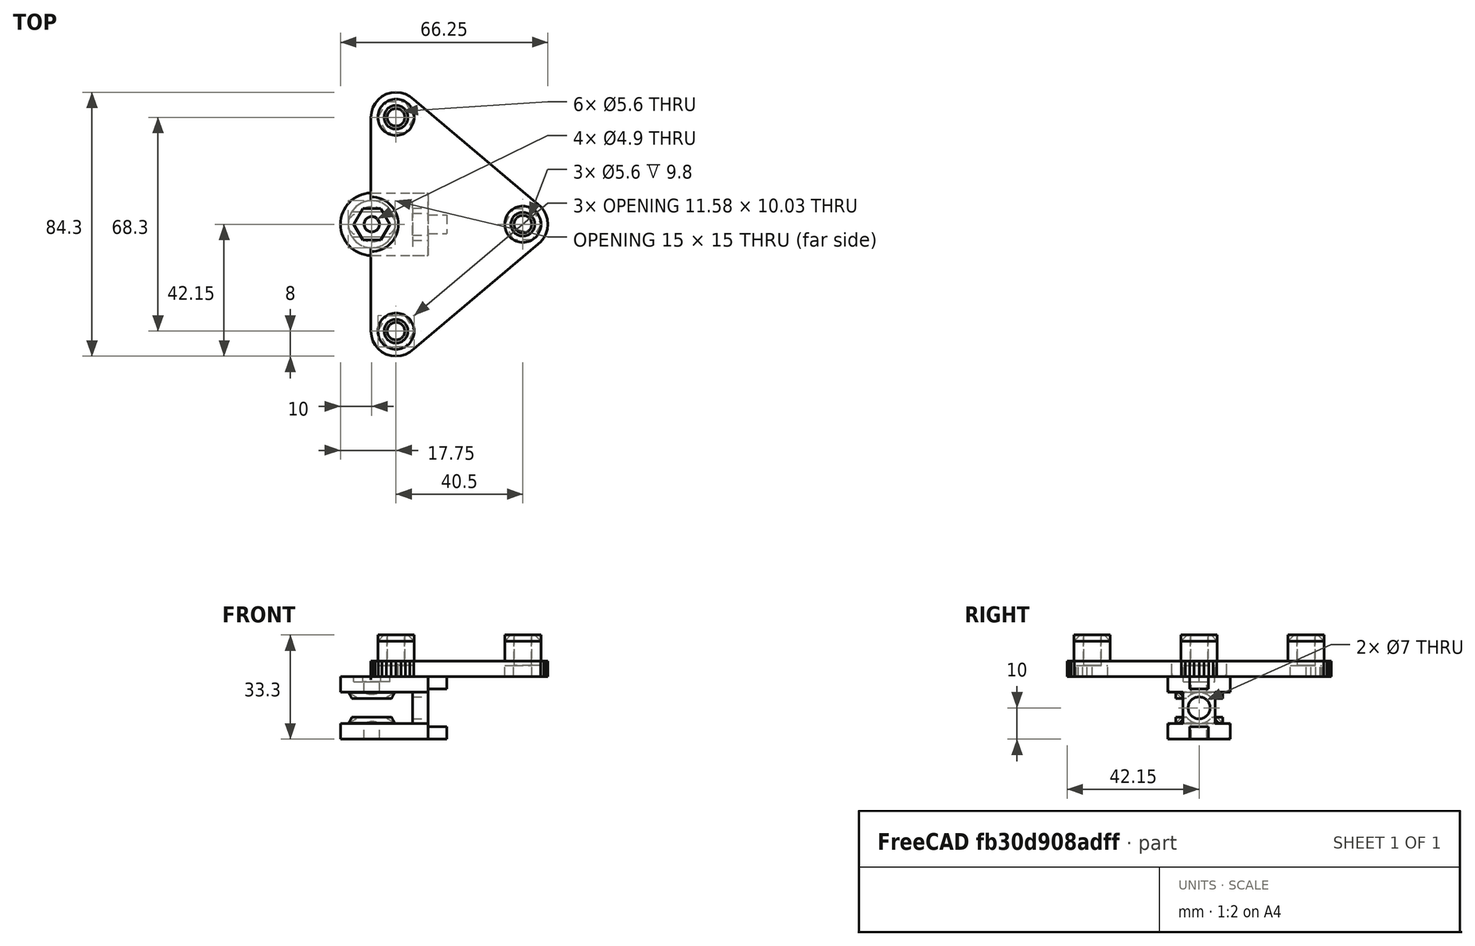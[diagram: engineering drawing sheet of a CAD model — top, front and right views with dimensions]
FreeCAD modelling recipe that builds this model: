
FCSTD DOCUMENT  (FreeCAD 0.19R24267 +99 (Git))
Label: carroZ_3
License: All rights reserved
LicenseURL: http://en.wikipedia.org/wiki/All_rights_reserved
objects: Part::Feature×36, Part::Cylinder×14, Part::Box×10, Part::Fillet×9, Part::Cut×8, Part::MultiFuse×8, Part::Chamfer×7, Part::Fuse×6, Part::Prism×4, Part::Part2DObjectPython×4, Part::FeaturePython×2, Part::Extrusion×1, Part::Common×1, App::DocumentObjectGroupPython×1, Part::Refine×1
note: 111 computed .brp shape members not serialized (recipe doc carries the construction recipe); baked Part::Feature solids carry a one-line shape summary decoded from their .brp

FEATURE [Part::Box] cube
  AttacherType = Attacher::AttachEngine3D
  Height = 5
  Length = 20
  Placement = pos=(-10,-10,0) rot=(0,0,1;0rad)
  Width = 20
FEATURE [Part::Cylinder] cylinder
  Angle = 360
  AttacherType = Attacher::AttachEngine3D
  Height = 100
  Placement = pos=(0,0,-50) rot=(0,0,1;0rad)
  Radius = 3.5
FEATURE [Part::Cut] difference
  Base = -> cube
  Tool = -> cylinder
FEATURE [Part::Box] cube001
  AttacherType = Attacher::AttachEngine3D
  Height = 11
  Length = 4
  Placement = pos=(6,-3,0) rot=(0,0,1;0rad)
  Width = 6
FEATURE [Part::Box] cube002
  AttacherType = Attacher::AttachEngine3D
  Height = 11
  Length = 4
  Placement = pos=(3,6,0) rot=(0,0,1;1.5708rad)
  Width = 6
FEATURE [Part::Box] cube003
  AttacherType = Attacher::AttachEngine3D
  Height = 11
  Length = 4
  Placement = pos=(-6,3,0) rot=(0,0,1;3.14159rad)
  Width = 6
FEATURE [Part::Box] cube004
  AttacherType = Attacher::AttachEngine3D
  Height = 11
  Length = 4
  Placement = pos=(-3,-6,0) rot=(0,0,-1;1.5708rad)
  Width = 6
FEATURE [Part::MultiFuse] Group
  Shapes = -> [cube001,cube002,cube003,cube004]
FEATURE [Part::Fuse] Group001
  Base = -> difference
  Tool = -> Group
FEATURE [Part::Box] cube005
  AttacherType = Attacher::AttachEngine3D
  Height = 100
  Length = 100
  Placement = pos=(5.15,-5,-50) rot=(0,0,1;0rad)
  Width = 10
FEATURE [Part::Box] cube006
  AttacherType = Attacher::AttachEngine3D
  Height = 100
  Length = 100
  Placement = pos=(-5.15,5,-50) rot=(0,0,1;3.14159rad)
  Width = 10
FEATURE [Part::Fuse] Group002
  Base = -> cube005
  Tool = -> cube006
FEATURE [Part::Cut] difference001
  Base = -> Group001
  Tool = -> Group002
FEATURE [Part::Box] cube007
  AttacherType = Attacher::AttachEngine3D
  Height = 13
  Length = 20
  Placement = pos=(-10,-10,-13) rot=(0,0,1;0rad)
  Width = 5
FEATURE [Part::Cylinder] cylinder001
  Angle = 360
  AttacherType = Attacher::AttachEngine3D
  Height = 5
  Placement = pos=(0,10,-13) rot=(1,0,0;1.5708rad)
  Radius = 10
FEATURE [Part::Cylinder] cylinder002
  Angle = 360
  AttacherType = Attacher::AttachEngine3D
  Height = 7
  Placement = pos=(0,10,-13) rot=(1,0,0;1.5708rad)
  Radius = 7.5
FEATURE [Part::MultiFuse] union
  Shapes = -> [cube007,cylinder001,cylinder002]
FEATURE [Part::Box] cube008
  AttacherType = Attacher::AttachEngine3D
  Height = 13
  Length = 20
  Placement = pos=(-10,-10,-13) rot=(0,0,1;0rad)
  Width = 5
FEATURE [Part::Cylinder] cylinder003
  Angle = 360
  AttacherType = Attacher::AttachEngine3D
  Height = 5
  Placement = pos=(0,10,-13) rot=(1,0,0;1.5708rad)
  Radius = 10
FEATURE [Part::Cylinder] cylinder004
  Angle = 360
  AttacherType = Attacher::AttachEngine3D
  Height = 7
  Placement = pos=(0,10,-13) rot=(1,0,0;1.5708rad)
  Radius = 7.5
FEATURE [Part::MultiFuse] union001
  Placement = pos=(0,0,0) rot=(0,0,1;3.14159rad)
  Shapes = -> [cube008,cylinder003,cylinder004]
FEATURE [Part::Fuse] Group003
  Base = -> union
  Tool = -> union001
FEATURE [Part::Cylinder] cylinder005
  Angle = 360
  AttacherType = Attacher::AttachEngine3D
  Height = 1000
  Placement = pos=(0,0,-500) rot=(0,0,1;0rad)
  Radius = 5
FEATURE [Part::Cylinder] cylinder006
  Angle = 360
  AttacherType = Attacher::AttachEngine3D
  Height = 1000
  Placement = pos=(0,500,-13) rot=(1,0,0;1.5708rad)
  Radius = 2.45
FEATURE [Part::Prism] prism
  AttacherType = Attacher::AttachEngine3D
  Circumradius = 5.79
  FirstAngle = 0
  Height = 5
  Placement = pos=(0,-8.33333,-13) rot=(0.57735,0.57735,-0.57735;2.0944rad)
  Polygon = 6
  SecondAngle = 0
FEATURE [Part::MultiFuse] union002
  Shapes = -> [cylinder005,cylinder006,prism]
FEATURE [Part::Cut] difference002
  Base = -> Group003
  Tool = -> union002
FEATURE [Part::Fuse] Group004
  Base = -> difference001
  Placement = pos=(-15,0,-10) rot=(-0.57735,0.57735,-0.57735;2.0944rad)
  Tool = -> difference002
FEATURE [Part::Feature] polygon
  shape: bbox 40.5 x 68.3 x 2e-07 mm, 1 faces, 0 solids (baked)
FEATURE [Part::Part2DObjectPython] circle  # Draft 2D object (typed FeaturePython)
  Area = 201.062
  FirstAngle = 0
  LastAngle = 0
  MakeFace = true
  Radius = 8
FEATURE [Part::FeaturePython] minkowski  # WARN: FeaturePython — macro-defined, semantics opaque (R4)
  Arguments = {'convexity': '0'}
  Children = -> [polygon,circle]
  Operation = minkowski
FEATURE [Part::Part2DObjectPython] circle001  # Draft 2D object (typed FeaturePython)
  Area = 24.6301
  FirstAngle = 0
  LastAngle = 0
  MakeFace = true
  Placement = pos=(-20.25,-34.15,0) rot=(0,0,1;0rad)
  Radius = 2.8
FEATURE [Part::Part2DObjectPython] circle002  # Draft 2D object (typed FeaturePython)
  Area = 24.6301
  FirstAngle = 0
  LastAngle = 0
  MakeFace = true
  Placement = pos=(-20.25,34.15,0) rot=(0,0,1;0rad)
  Radius = 2.8
FEATURE [Part::Part2DObjectPython] circle003  # Draft 2D object (typed FeaturePython)
  Area = 24.6301
  FirstAngle = 0
  LastAngle = 0
  MakeFace = true
  Placement = pos=(20.25,0,0) rot=(0,0,1;0rad)
  Radius = 2.8
FEATURE [Part::MultiFuse] union003
  Shapes = -> [circle001,circle002,circle003]
FEATURE [Part::Cut] difference003
  Base = -> minkowski
  Tool = -> union003
FEATURE [Part::FeaturePython] RefineLinearExtrude  # WARN: FeaturePython — macro-defined, semantics opaque (R4)
  Base = -> difference003
FEATURE [Part::Extrusion] LinearExtrude
  Base = -> RefineLinearExtrude
  Dir = (0,0,5)
  DirMode = 0
  FaceMakerClass = Part::FaceMakerBullseye
  LengthFwd = 0
  LengthRev = 0
  Solid = false
  Symmetric = false
FEATURE [Part::Cylinder] cylinder007
  Angle = 360
  AttacherType = Attacher::AttachEngine3D
  Height = 13.3
  Radius = 5.8
FEATURE [Part::Cylinder] cylinder008
  Angle = 360
  AttacherType = Attacher::AttachEngine3D
  Height = 53.2
  Placement = pos=(0,0,-26.6) rot=(0,0,1;0rad)
  Radius = 2.8
FEATURE [Part::Cut] difference004
  Base = -> cylinder007
  Placement = pos=(-20.25,-34.15,0) rot=(0,0,1;0rad)
  Tool = -> cylinder008
FEATURE [Part::Cylinder] cylinder009
  Angle = 360
  AttacherType = Attacher::AttachEngine3D
  Height = 13.3
  Radius = 5.8
FEATURE [Part::Cylinder] cylinder010
  Angle = 360
  AttacherType = Attacher::AttachEngine3D
  Height = 53.2
  Placement = pos=(0,0,-26.6) rot=(0,0,1;0rad)
  Radius = 2.8
FEATURE [Part::Cut] difference005
  Base = -> cylinder009
  Placement = pos=(-20.25,34.15,0) rot=(0,0,1;0rad)
  Tool = -> cylinder010
FEATURE [Part::Cylinder] cylinder011
  Angle = 360
  AttacherType = Attacher::AttachEngine3D
  Height = 13.3
  Radius = 5.8
FEATURE [Part::Cylinder] cylinder012
  Angle = 360
  AttacherType = Attacher::AttachEngine3D
  Height = 53.2
  Placement = pos=(0,0,-26.6) rot=(0,0,1;0rad)
  Radius = 2.8
FEATURE [Part::Cut] difference006
  Base = -> cylinder011
  Placement = pos=(20.25,0,0) rot=(0,0,1;0rad)
  Tool = -> cylinder012
FEATURE [Part::MultiFuse] union004
  Shapes = -> [LinearExtrude,difference004,difference005,difference006]
FEATURE [Part::Prism] prism001
  AttacherType = Attacher::AttachEngine3D
  Circumradius = 5.79
  FirstAngle = 0
  Height = 7
  Placement = pos=(-20.25,-34.15,-3.5) rot=(0,0,1;0rad)
  Polygon = 6
  SecondAngle = 0
FEATURE [Part::Prism] prism002
  AttacherType = Attacher::AttachEngine3D
  Circumradius = 5.79
  FirstAngle = 0
  Height = 7
  Placement = pos=(-20.25,34.15,-3.5) rot=(0,0,1;0rad)
  Polygon = 6
  SecondAngle = 0
FEATURE [Part::Prism] prism003
  AttacherType = Attacher::AttachEngine3D
  Circumradius = 5.79
  FirstAngle = 0
  Height = 7
  Placement = pos=(20.25,0,-3.5) rot=(0,0,1;0rad)
  Polygon = 6
  SecondAngle = 0
FEATURE [Part::MultiFuse] Group005
  Shapes = -> [prism001,prism002,prism003]
FEATURE [Part::Cylinder] cylinder013
  Angle = 360
  AttacherType = Attacher::AttachEngine3D
  Height = 100
  Placement = pos=(-28.25,0,-50) rot=(0,0,1;0rad)
  Radius = 8.75
FEATURE [Part::Fuse] union005
  Base = -> Group005
  Tool = -> cylinder013
FEATURE [Part::Cut] difference007
  Base = -> union004
  Tool = -> union005
FEATURE [Part::Box] cube009
  AttacherType = Attacher::AttachEngine3D
  Height = 200
  Length = 200
  Placement = pos=(-100,-100,-100) rot=(0,0,1;0rad)
  Width = 200
FEATURE [Part::Common] intersection
  Base = -> difference007
  Tool = -> cube009
FEATURE [Part::Fuse] Group006
  Base = -> Group004
  Tool = -> intersection
FEATURE [App::DocumentObjectGroupPython] LayerContainer  label="Capas"  # scripted group (container) (typed FeaturePython)
FEATURE [Part::Feature] Line
  shape: bbox 1.561 x 0.1533 x 2e-07 mm, 0 faces, 0 solids (baked)
FEATURE [Part::Feature] Line001
  shape: bbox 1.561 x 0.1533 x 2e-07 mm, 0 faces, 0 solids (baked)
FEATURE [Part::Feature] Line002
  shape: bbox 1.501 x 0.4561 x 2e-07 mm, 0 faces, 0 solids (baked)
FEATURE [Part::Feature] Line003
  shape: bbox 1.383 x 0.7392 x 2e-07 mm, 0 faces, 0 solids (baked)
FEATURE [Part::Feature] Line004
  shape: bbox 1.213 x 0.9942 x 2e-07 mm, 0 faces, 0 solids (baked)
FEATURE [Part::Feature] Line005
  shape: bbox 0.9942 x 1.213 x 2e-07 mm, 0 faces, 0 solids (baked)
FEATURE [Part::Feature] Line006
  shape: bbox 0.7392 x 1.383 x 2e-07 mm, 0 faces, 0 solids (baked)
FEATURE [Part::Feature] Line007
  shape: bbox 0.4561 x 1.501 x 2e-07 mm, 0 faces, 0 solids (baked)
FEATURE [Part::Feature] Line008
  shape: bbox 0.1533 x 1.561 x 2e-07 mm, 0 faces, 0 solids (baked)
FEATURE [Part::Feature] Line009
  shape: bbox 2e-07 x 68.3 x 2e-07 mm, 0 faces, 0 solids (baked)
FEATURE [Part::Feature] Line010
  shape: bbox 0.1533 x 1.561 x 2e-07 mm, 0 faces, 0 solids (baked)
FEATURE [Part::Feature] Line011
  shape: bbox 0.4561 x 1.501 x 2e-07 mm, 0 faces, 0 solids (baked)
FEATURE [Part::Feature] Line012
  shape: bbox 0.7392 x 1.383 x 2e-07 mm, 0 faces, 0 solids (baked)
FEATURE [Part::Feature] Line013
  shape: bbox 0.9942 x 1.213 x 2e-07 mm, 0 faces, 0 solids (baked)
FEATURE [Part::Feature] Line014
  shape: bbox 1.213 x 0.9942 x 2e-07 mm, 0 faces, 0 solids (baked)
FEATURE [Part::Feature] Line015
  shape: bbox 1.383 x 0.7392 x 2e-07 mm, 0 faces, 0 solids (baked)
FEATURE [Part::Feature] Line016
  shape: bbox 1.501 x 0.4561 x 2e-07 mm, 0 faces, 0 solids (baked)
FEATURE [Part::Feature] Line017
  shape: bbox 1.561 x 0.1533 x 2e-07 mm, 0 faces, 0 solids (baked)
FEATURE [Part::Feature] Line018
  shape: bbox 1.561 x 0.1533 x 2e-07 mm, 0 faces, 0 solids (baked)
FEATURE [Part::Feature] Line019
  shape: bbox 1.501 x 0.4561 x 2e-07 mm, 0 faces, 0 solids (baked)
FEATURE [Part::Feature] Line020
  shape: bbox 1.383 x 0.7392 x 2e-07 mm, 0 faces, 0 solids (baked)
FEATURE [Part::Feature] Line021
  shape: bbox 1.213 x 0.9942 x 2e-07 mm, 0 faces, 0 solids (baked)
FEATURE [Part::Feature] Line022
  shape: bbox 40.5 x 34.15 x 2e-07 mm, 0 faces, 0 solids (baked)
FEATURE [Part::Feature] Line023
  shape: bbox 0.9942 x 1.213 x 2e-07 mm, 0 faces, 0 solids (baked)
FEATURE [Part::Feature] Line024
  shape: bbox 0.7392 x 1.383 x 2e-07 mm, 0 faces, 0 solids (baked)
FEATURE [Part::Feature] Line025
  shape: bbox 0.4561 x 1.501 x 2e-07 mm, 0 faces, 0 solids (baked)
FEATURE [Part::Feature] Line026
  shape: bbox 0.1533 x 1.561 x 2e-07 mm, 0 faces, 0 solids (baked)
FEATURE [Part::Feature] Line027
  shape: bbox 0.1533 x 1.561 x 2e-07 mm, 0 faces, 0 solids (baked)
FEATURE [Part::Feature] Line028
  shape: bbox 0.4561 x 1.501 x 2e-07 mm, 0 faces, 0 solids (baked)
FEATURE [Part::Feature] Line029
  shape: bbox 0.7392 x 1.383 x 2e-07 mm, 0 faces, 0 solids (baked)
FEATURE [Part::Feature] Line030
  shape: bbox 0.9942 x 1.213 x 2e-07 mm, 0 faces, 0 solids (baked)
FEATURE [Part::Feature] Line031
  shape: bbox 40.5 x 34.15 x 2e-07 mm, 0 faces, 0 solids (baked)
FEATURE [Part::Feature] Line032
  shape: bbox 1.213 x 0.9942 x 2e-07 mm, 0 faces, 0 solids (baked)
FEATURE [Part::Feature] Line033
  shape: bbox 1.383 x 0.7392 x 2e-07 mm, 0 faces, 0 solids (baked)
FEATURE [Part::Feature] Line034
  shape: bbox 1.501 x 0.4561 x 2e-07 mm, 0 faces, 0 solids (baked)
FEATURE [Part::MultiFuse] Fusion
  Shapes = -> [Group004,intersection]
FEATURE [Part::Refine] Fusion001
  Source = -> Fusion
FEATURE [Part::Fillet] Fillet
  Base = -> Fusion001
  Edges = 1 edges r=1: [Edge283]
FEATURE [Part::Chamfer] Chamfer
  Base = -> Fillet
  Edges = 1 edges r=2: [Edge169]
FEATURE [Part::Chamfer] Chamfer001
  Base = -> Chamfer
  Edges = 1 edges r=2: [Edge133]
FEATURE [Part::Chamfer] Chamfer002
  Base = -> Chamfer001
  Edges = 1 edges r=2: [Edge131]
FEATURE [Part::Fillet] Fillet001
  Base = -> Chamfer002
  Edges = 1 edges r=2: [Edge261]
FEATURE [Part::Fillet] Fillet002
  Base = -> Fillet001
  Edges = 1 edges r=2: [Edge23]
FEATURE [Part::Fillet] Fillet003
  Base = -> Fillet002
  Edges = 1 edges r=2: [Edge35]
FEATURE [Part::Fillet] Fillet004
  Base = -> Fillet003
  Edges = 1 edges r=2: [Edge25]
FEATURE [Part::Chamfer] Chamfer003
  Base = -> Fillet004
  Edges = 1 edges r=1.9: [Edge153]
FEATURE [Part::Chamfer] Chamfer004
  Base = -> Chamfer003
  Edges = 1 edges r=1.9: [Edge28]
FEATURE [Part::Chamfer] Chamfer005
  Base = -> Chamfer004
  Edges = 1 edges r=1.9: [Edge199]
FEATURE [Part::Chamfer] Chamfer006
  Base = -> Chamfer005
  Edges = 1 edges r=1.9: [Edge30]
FEATURE [Part::Fillet] Fillet005
  Base = -> Chamfer006
  Edges = 1 edges r=1: [Edge43]
FEATURE [Part::Fillet] Fillet006
  Base = -> Fillet005
  Edges = 1 edges r=1: [Edge57]
FEATURE [Part::Fillet] Fillet007
  Base = -> Fillet006
  Edges = 1 edges r=1: [Edge68]
FEATURE [Part::Fillet] Fillet008
  Base = -> Fillet007
  Edges = 1 edges r=1: [Edge175]
